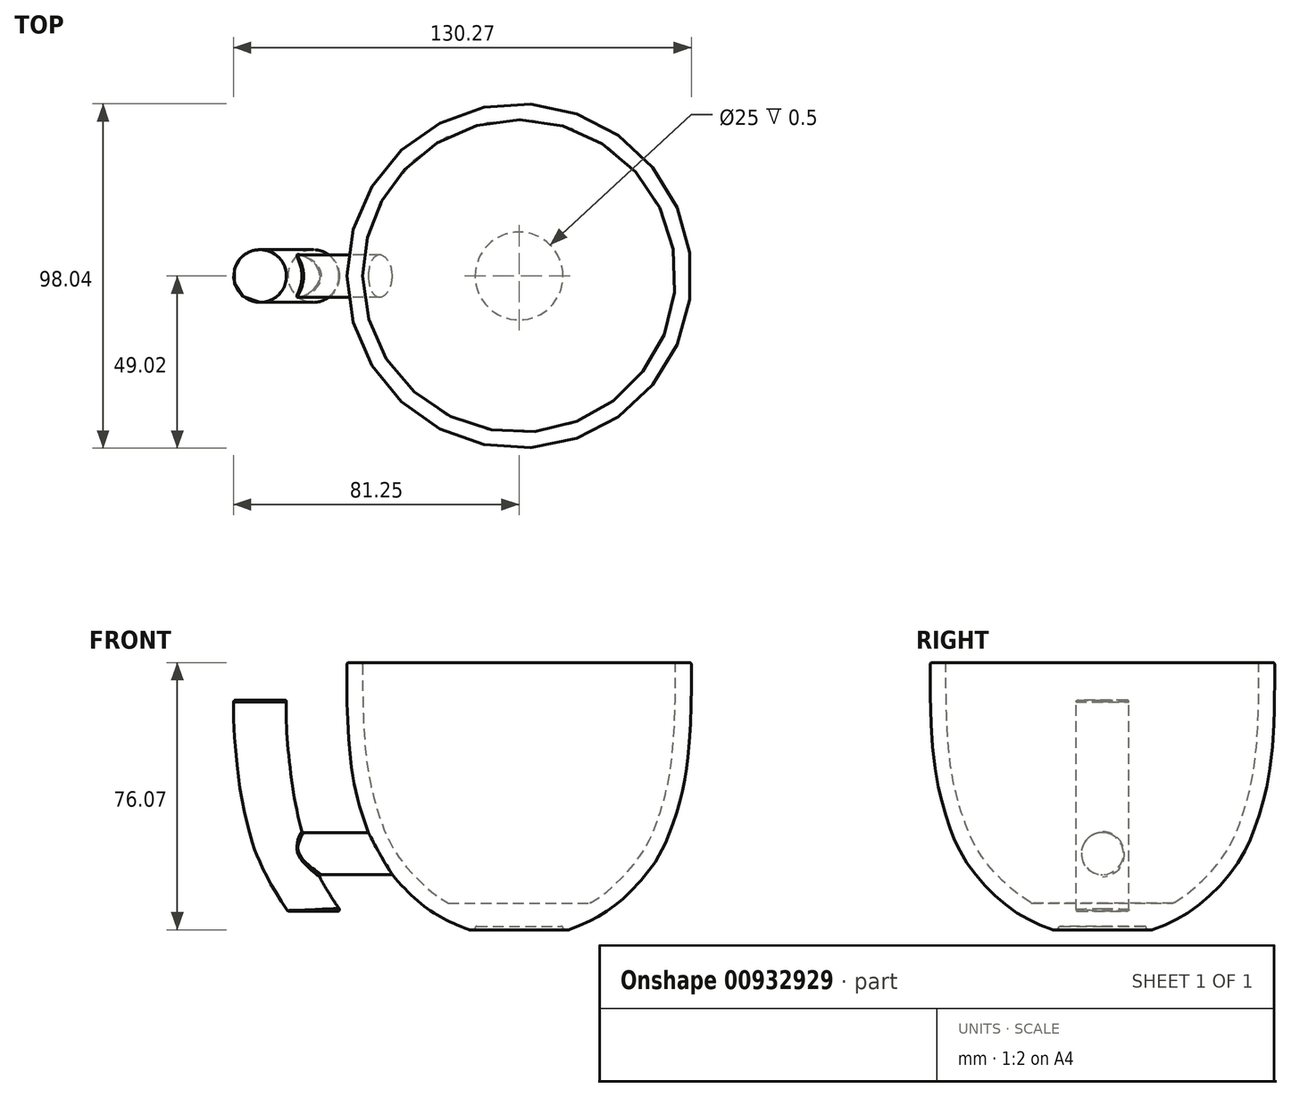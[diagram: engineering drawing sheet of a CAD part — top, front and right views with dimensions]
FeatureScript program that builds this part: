
annotation { "Feature Type Name" : "Feature", "Feature Type Description" : "" }
export const myFeature = defineFeature(function(context is Context, id is Id, definition is map)
    precondition{}
    {
        {
            var Q0;
            Q0=qCreatedBy(makeId("Front.planeOp"),FACE);
            var sketch = newSketch(context, id + "F0", { "sketchPlane" : qUnion([Q0])});
            skLineSegment(sketch, "E0", {"start": v(0, 78.82) * mm, "end": v(-49, 78.82) * mm});
            skLineSegment(sketch, "E1", {"start": v(0, 0) * mm, "end": v(0, 78.82) * mm});
            skFitSpline(sketch, "E2", {"points": [v(-49, 78.82) * mm, v(-49, 71.2) * mm, v(-47.95, 50.94) * mm, v(-44.24, 34.32) * mm, v(-38.54, 21.8) * mm, v(-27.37, 9.77) * mm, v(-17.3, 3.96) * mm, v(0, 0) * mm], "startDerivative": vector(-0.53, -120.05) * mm, "endDerivative": vector(126.32, 0) * mm});
            skSolve(sketch);
        }
        {
            var Q0;
            Q0=qSketchRegion(id+"F0",true);
            var Q1;
            Q1=sQuery(id+"F0.wireOp",EDGE,"E1");
            revolve(context, id + "F1", {"surfaceOperationType" : NewSurfaceOperationType.NEW, "entities" : qUnion([Q0]), "axis" : qUnion([Q1]), "revolveType" : RevolveType.FULL});
        }
        {
            var Q0;
            Q0=makeQuery(id+"F1.opRevolve","SWEPT_FACE",FACE,{"disambiguationData":[OSD([sQuery(id+"F0.wireOp",EDGE,"E0")])]});
            shell(context, id + "F2", {"entities" : qUnion([Q0]), "thickness" : 4.5 * mm});
        }
        {
            var Q0;
            Q0=makeQuery(id+"F1.opRevolve","SWEPT_EDGE",EDGE,{"disambiguationData":[OSD([sQuery(id+"F0.wireOp",EDGE,"E0"),sQuery(id+"F0.wireOp",EDGE,"E2")])]});
            var Q1;
            Q1=makeQuery(id+"F2.opShell","OFFSET_EDGE",EDGE,{"disambiguationData":[OSD([sQuery(id+"F0.wireOp",EDGE,"E0"),sQuery(id+"F0.wireOp",EDGE,"E2")])]});
            fillet(context, id + "F3", {"entities" : qUnion([Q0, Q1]), "radius" : .5 * mm, "tangentPropagation" : true, "defaultsChanged" : true, "vertexSettings" : [], "allowEdgeOverflow" : false});
        }
        {
            var Q0;
            Q0=qCreatedBy(makeId("Front.planeOp"),FACE);
            var sketch = newSketch(context, id + "F4", { "sketchPlane" : qUnion([Q0])});
            skLineSegment(sketch, "E3", {"start": v(-41.77, 30.38) * mm, "end": v(-53.43, 30.38) * mm});
            skLineSegment(sketch, "E4", {"start": v(-49.23, 20.12) * mm, "end": v(-36.53, 20.12) * mm});
            skLineSegment(sketch, "E5", {"start": v(-36.53, 20.12) * mm, "end": v(-41.77, 30.38) * mm});
            skFitSpline(sketch, "E6", {"points": [v(-42.03, 8) * mm, v(-47.44, 16.94) * mm, v(-49.23, 20.12) * mm, v(-51.33, 24.44) * mm, v(-53.43, 30.38) * mm, v(-55.23, 38.72) * mm, v(-56.67, 49.18) * mm, v(-57.32, 61.86) * mm, v(-57.58, 68.13) * mm, v(-57.6, 68.09) * mm], "startDerivative": vector(-47.1, 69.03) * mm, "endDerivative": vector(-6.03, -13.35) * mm});
            skLineSegment(sketch, "E7", {"start": v(-57.58, 68.13) * mm, "end": v(-69.83, 68.13) * mm});
            skFitSpline(sketch, "E8", {"points": [v(-69.83, 68.13) * mm, v(-69.83, 61.07) * mm, v(-69.06, 51.29) * mm, v(-67.63, 40.46) * mm, v(-65.54, 31.18) * mm, v(-63.64, 25) * mm, v(-58.64, 14.66) * mm, v(-54.3, 8) * mm], "startDerivative": vector(-1.12, -53.42) * mm, "endDerivative": vector(31.44, -44.67) * mm});
            skLineSegment(sketch, "E9", {"start": v(-54.3, 8) * mm, "end": v(-42.03, 8) * mm});
            skSolve(sketch);
        }
        {
            var Q0;
            Q0=qCreatedBy(makeId("Right.planeOp"),FACE);
            cPlane(context, id + "F5", {"entities" : qUnion([Q0]), "cplaneType" : CPlaneType.OFFSET, "offset" : 65 * mm, "oppositeDirection" : true, "width" : 150 * mm, "height" : 150 * mm});
        }
        {
            var Q0;
            Q0=qCreatedBy(id+"F5.planeOp",FACE);
            var sketch = newSketch(context, id + "F6", { "sketchPlane" : qUnion([Q0])});
            skPoint(sketch, "E10.middle", {"position": v(0, 24.44) * mm});
            skCircle(sketch, "E11", {"center": v(0, 24.44) * mm, "radius": 6 * mm});
            skSolve(sketch);
        }
        {
            var Q0;
            Q0=qSketchRegion(id+"F6",true);
            extrude(context, id + "F7", {"entities" : qUnion([Q0]), "operationType" : NewBodyOperationType.ADD, "endBound" : BoundingType.UP_TO_NEXT, "depth" : 25 * mm, "offsetDistance" : 25 * mm});
        }
        {
            var Q0;
            Q0=qCreatedBy(makeId("Top.planeOp"),FACE);
            cPlane(context, id + "F8", {"entities" : qUnion([Q0]), "cplaneType" : CPlaneType.OFFSET, "offset" : 8 * mm, "width" : 150 * mm, "height" : 150 * mm});
        }
        {
            var Q0;
            Q0=qCreatedBy(id+"F8.planeOp",FACE);
            var sketch = newSketch(context, id + "F9", { "sketchPlane" : qUnion([Q0])});
            skPoint(sketch, "E12.middle", {"position": v(-58.17, 0) * mm});
            skCircle(sketch, "E13", {"center": v(-58.17, 0) * mm, "radius": 7.5 * mm});
            skSolve(sketch);
        }
        {
            var Q0;
            Q0=qSketchRegion(id+"F9",true);
            var Q1;
            Q1=sQuery(id+"F4.wireOp",EDGE,"E8");
            sweep(context, id + "F10", {"operationType" : NewBodyOperationType.ADD, "profiles" : qUnion([Q0]), "path" : qUnion([Q1]), "keepProfileOrientation" : true});
        }
        {
            var Q0;
            Q0=makeQuery(id+"F10.opSweep","CAP_FACE",FACE,{"disambiguationData":[OSD([sQuery(id+"F4.wireOp",VERTEX,"E8.start"),sQuery(id+"F9.wireOp",EDGE,"E12.bottom"),sQuery(id+"F9.wireOp",EDGE,"E12.top"),sQuery(id+"F9.wireOp",EDGE,"E12.left"),sQuery(id+"F9.wireOp",EDGE,"E12.right")])],"isStart":false});
            var Q1;
            Q1=makeQuery(id+"F10.opSweep","CAP_FACE",FACE,{"disambiguationData":[OSD([sQuery(id+"F4.wireOp",VERTEX,"E8.end"),sQuery(id+"F9.wireOp",EDGE,"E12.bottom"),sQuery(id+"F9.wireOp",EDGE,"E12.top"),sQuery(id+"F9.wireOp",EDGE,"E12.left"),sQuery(id+"F9.wireOp",EDGE,"E12.right")])],"isStart":true});
            fillet(context, id + "F11", {"entities" : qUnion([Q0, Q1]), "radius" : .5 * mm, "tangentPropagation" : true, "defaultsChanged" : true, "vertexSettings" : [], "allowEdgeOverflow" : false});
        }
        {
            var Q0;
            Q0=qCreatedBy(makeId("Front.planeOp"),FACE);
            var sketch = newSketch(context, id + "F12", { "sketchPlane" : qUnion([Q0])});
            skLineSegment(sketch, "E14", {"start": v(0, 1.35) * mm, "end": v(0, 10.35) * mm});
            skLineSegment(sketch, "E15", {"start": v(0, 10.35) * mm, "end": v(-22, 10.35) * mm});
            skLineSegment(sketch, "E16", {"start": v(-22, 10.35) * mm, "end": v(0, 1.35) * mm});
            skSolve(sketch);
        }
        {
            var Q0;
            Q0=qSketchRegion(id+"F12",true);
            var Q1;
            Q1=sQuery(id+"F12.wireOp",EDGE,"E14");
            revolve(context, id + "F13", {"operationType" : NewBodyOperationType.ADD, "surfaceOperationType" : NewSurfaceOperationType.NEW, "entities" : qUnion([Q0]), "axis" : qUnion([Q1]), "revolveType" : RevolveType.FULL});
        }
        {
            var Q0;
            Q0=qCreatedBy(makeId("Front.planeOp"),FACE);
            var sketch = newSketch(context, id + "F14", { "sketchPlane" : qUnion([Q0])});
            skLineSegment(sketch, "E17.bottom", {"start": v(20, 0) * mm, "end": v(-20, 0) * mm});
            skLineSegment(sketch, "E17.top", {"start": v(20, 2.75) * mm, "end": v(-20, 2.75) * mm});
            skLineSegment(sketch, "E17.left", {"start": v(20, 0) * mm, "end": v(20, 2.75) * mm});
            skLineSegment(sketch, "E17.right", {"start": v(-20, 0) * mm, "end": v(-20, 2.75) * mm});
            skSolve(sketch);
        }
        {
            var Q0;
            Q0=qSketchRegion(id+"F14",true);
            extrude(context, id + "F15", {"entities" : qUnion([Q0]), "operationType" : NewBodyOperationType.REMOVE, "oppositeDirection" : true, "depth" : 40 * mm, "offsetDistance" : 25 * mm, "symmetric" : true});
        }
        {
            var Q0;
            Q0=makeQuery(id+"F15.boolean.opBoolean","COPY",FACE,{"derivedFrom":makeQuery(id+"F15.opExtrude","SWEPT_FACE",FACE,{"disambiguationData":[OSD([sQuery(id+"F14.wireOp",EDGE,"E17.top")])]})});
            var sketch = newSketch(context, id + "F16", { "sketchPlane" : qUnion([Q0])});
            skCircle(sketch, "E18", {"center": v(0, 0) * mm, "radius": 12.5 * mm});
            skSolve(sketch);
        }
        {
            var Q0;
            Q0=makeQuery(id+"F16.imprint","IMPRINT",FACE,{"disambiguationData":[TD([[makeQuery(id+"F16.imprint","IMPRINT",EDGE,{"derivedFrom":sQuery(id+"F16.wireOp",EDGE,"E18")}),1.0]])]});
            extrude(context, id + "F17", {"entities" : qUnion([Q0]), "operationType" : NewBodyOperationType.REMOVE, "oppositeDirection" : true, "depth" : 1 * mm, "offsetDistance" : 25 * mm});
        }
        {
            var Q0;
            Q0=makeQuery(id+"F15.boolean.opBoolean","INTERSECT",EDGE,{"derivedFrom":[makeQuery(id+"F1.opRevolve","SWEPT_FACE",FACE,{"disambiguationData":[OSD([sQuery(id+"F0.wireOp",EDGE,"E2")])]}),makeQuery(id+"F15.opExtrude","SWEPT_FACE",FACE,{"disambiguationData":[OSD([sQuery(id+"F14.wireOp",EDGE,"E17.top")])]})]});
            var Q1;
            Q1=makeQuery(id+"F13.boolean.opBoolean","INTERSECT",EDGE,{"derivedFrom":[makeQuery(id+"F2.opShell","OFFSET_FACE",FACE,{"disambiguationData":[OSD([sQuery(id+"F0.wireOp",EDGE,"E2")])]}),makeQuery(id+"F13.opRevolve","SWEPT_FACE",FACE,{"disambiguationData":[OSD([sQuery(id+"F12.wireOp",EDGE,"E15")])]})]});
            var Q2;
            Q2=makeQuery(id+"F17.boolean.opBoolean","COPY",EDGE,{"derivedFrom":makeQuery(id+"F17.opExtrude","CAP_EDGE",EDGE,{"disambiguationData":[OSD([sQuery(id+"F16.wireOp",EDGE,"E18")])],"isStart":true})});
            var Q3;
            Q3=makeQuery(id+"F17.boolean.opBoolean","COPY",EDGE,{"derivedFrom":makeQuery(id+"F17.opExtrude","CAP_EDGE",EDGE,{"disambiguationData":[OSD([sQuery(id+"F16.wireOp",EDGE,"E18")])],"isStart":false})});
            fillet(context, id + "F18", {"entities" : qUnion([Q0, Q1, Q2, Q3]), "tangentPropagation" : true, "radius" : .5 * mm, "defaultsChanged" : false, "vertexSettings" : [], "allowEdgeOverflow" : false});
        }
        {
            var Q0;
            Q0=makeQuery(id+"F7.opExtrude","CAP_EDGE",EDGE,{"disambiguationData":[OSD([sQuery(id+"F6.wireOp",EDGE,"E11")])],"isStart":false});
            var Q1;
            Q1=makeQuery(id+"F10.boolean.opBoolean","INTERSECT",EDGE,{"derivedFrom":[makeQuery(id+"F7.opExtrude","SWEPT_FACE",FACE,{"disambiguationData":[OSD([sQuery(id+"F6.wireOp",EDGE,"E11")])]}),makeQuery(id+"F10.opSweep","SWEPT_FACE",FACE,{"disambiguationData":[OSD([sQuery(id+"F4.wireOp",EDGE,"E8"),sQuery(id+"F9.wireOp",EDGE,"E13")])]})]});
            fillet(context, id + "F19", {"entities" : qUnion([Q0, Q1]), "tangentPropagation" : true, "radius" : .5 * mm, "defaultsChanged" : true, "vertexSettings" : [], "allowEdgeOverflow" : false});
        }
    });
